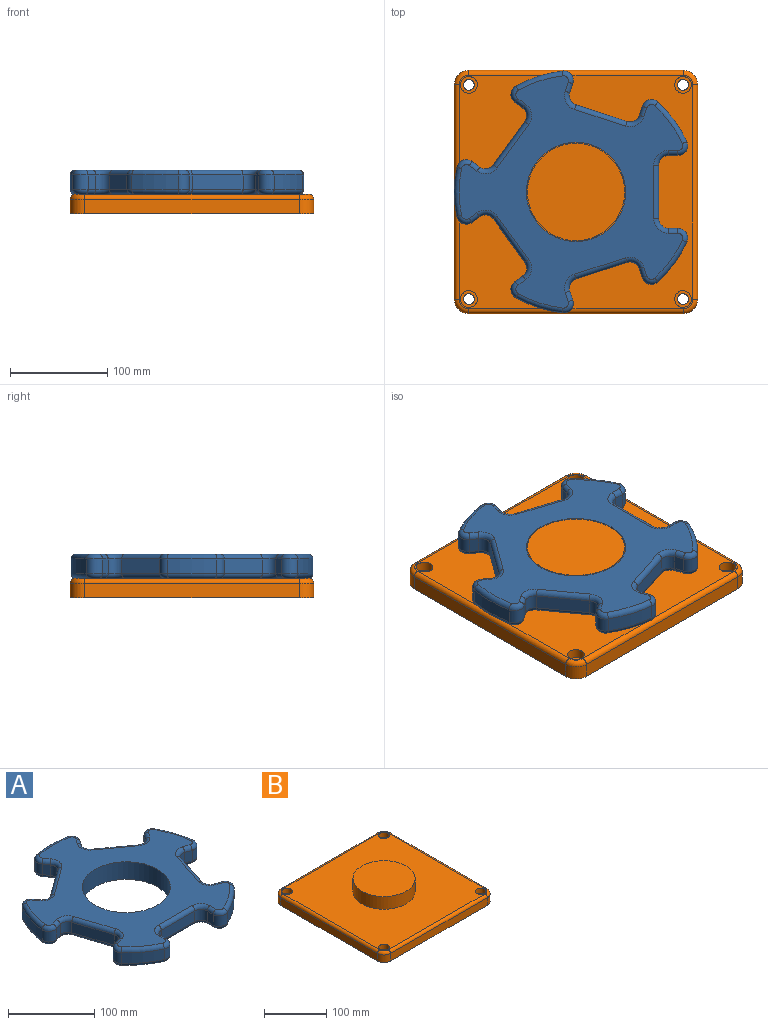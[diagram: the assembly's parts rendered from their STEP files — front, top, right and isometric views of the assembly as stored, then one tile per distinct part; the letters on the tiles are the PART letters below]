
ASSEMBLY  parts=2 mates=1
PART A: 123 faces, bbox 268.9x258.5x25 mm
  f0: plane 238.57x229.73mm, normal (0,0,1), area 21505.7mm2, adj f6,f43,f44,f45,f46,f47,f48,f49
  f1: plane 238.57x229.73mm, normal (0,0,-1), area 21505.7mm2, adj f6,f83,f84,f85,f86,f87,f88,f89
  f2: cylinder r=125mm len=40.68mm, axis (0,0,-1), area 759.5mm2, adj f13,f42,f51,f91
  f3: cylinder r=125mm len=47.82mm, axis (0,0,-1), area 759.5mm2, adj f35,f41,f67,f107
  f4: cylinder r=125mm len=50.29mm, axis (0,0,-1), area 759.5mm2, adj f28,f34,f82,f122
  f5: cylinder r=125mm len=47.82mm, axis (0,0,-1), area 759.5mm2, adj f21,f27,f66,f106
  f6: cylinder r=51mm len=102mm, axis (0,0,-1), area 8011.1mm2, adj f0,f1
  f7: cylinder r=125mm len=40.68mm, axis (0,0,-1), area 759.5mm2, adj f14,f20,f50,f90
  f8: plane 15x9.73mm, normal (-1,0,0), area 146mm2, adj f11,f14,f46,f86
  f9: plane 55x15mm, normal (0,-1,0), area 825mm2, adj f11,f12,f43,f83
  f10: plane 15x9.73mm, normal (1,0,0), area 146mm2, adj f12,f13,f47,f87
  f11: cylinder r=10mm len=15mm, axis (0,0,-1), area 235.6mm2, adj f8,f9,f44,f84
  f12: cylinder r=10mm len=15mm, axis (0,0,-1), area 235.6mm2, adj f9,f10,f45,f85
  f13: cylinder r=10mm len=15mm, axis (0,0,-1), area 299.5mm2, adj f2,f10,f49,f89
  f14: cylinder r=10mm len=15mm, axis (0,0,-1), area 299.5mm2, adj f7,f8,f48,f88
  f15: plane 15x9.26mm, normal (-0.31,-0.95,0), area 146mm2, adj f18,f21,f62,f102
  f16: plane 52.31x17mm, normal (0.95,-0.31,0), area 825mm2, adj f18,f19,f58,f98
  f17: plane 15x9.26mm, normal (0.31,0.95,0), area 146mm2, adj f19,f20,f54,f94
  f18: cylinder r=10mm len=15mm, axis (0,0,-1), area 235.6mm2, adj f15,f16,f60,f100
  f19: cylinder r=10mm len=15mm, axis (0,0,-1), area 235.6mm2, adj f16,f17,f56,f96
  f20: cylinder r=10mm len=16.25mm, axis (0,0,-1), area 299.5mm2, adj f7,f17,f52,f92
  f21: cylinder r=10mm len=15mm, axis (0,0,-1), area 299.5mm2, adj f5,f15,f64,f104
  f22: plane 15x7.87mm, normal (0.81,-0.59,0), area 146mm2, adj f25,f28,f78,f118
  f23: plane 44.5x32.33mm, normal (0.59,0.81,0), area 825mm2, adj f25,f26,f74,f114
  f24: plane 15x7.87mm, normal (-0.81,0.59,0), area 146mm2, adj f26,f27,f70,f110
  f25: cylinder r=10mm len=15mm, axis (0,0,-1), area 235.6mm2, adj f22,f23,f76,f116
  f26: cylinder r=10mm len=15mm, axis (0,0,-1), area 235.6mm2, adj f23,f24,f72,f112
  f27: cylinder r=10mm len=16.78mm, axis (0,0,-1), area 299.5mm2, adj f5,f24,f68,f108
  f28: cylinder r=10mm len=15.67mm, axis (0,0,-1), area 299.5mm2, adj f4,f22,f80,f120
  f29: plane 15x7.87mm, normal (0.81,0.59,0), area 146mm2, adj f32,f35,f71,f111
  f30: plane 44.5x32.33mm, normal (-0.59,0.81,0), area 825mm2, adj f32,f33,f75,f115
  f31: plane 15x7.87mm, normal (-0.81,-0.59,0), area 146mm2, adj f33,f34,f79,f119
  f32: cylinder r=10mm len=15mm, axis (0,0,-1), area 235.6mm2, adj f29,f30,f73,f113
  f33: cylinder r=10mm len=15mm, axis (0,0,-1), area 235.6mm2, adj f30,f31,f77,f117
  f34: cylinder r=10mm len=15.67mm, axis (0,0,-1), area 299.5mm2, adj f4,f31,f81,f121
  f35: cylinder r=10mm len=16.78mm, axis (0,0,-1), area 299.5mm2, adj f3,f29,f69,f109
  f36: plane 15x9.26mm, normal (-0.31,0.95,0), area 146mm2, adj f39,f42,f55,f95
  f37: plane 52.31x17mm, normal (-0.95,-0.31,0), area 825mm2, adj f39,f40,f59,f99
  f38: plane 15x9.26mm, normal (0.31,-0.95,0), area 146mm2, adj f40,f41,f63,f103
  f39: cylinder r=10mm len=15mm, axis (0,0,-1), area 235.6mm2, adj f36,f37,f57,f97
  f40: cylinder r=10mm len=15mm, axis (0,0,-1), area 235.6mm2, adj f37,f38,f61,f101
  f41: cylinder r=10mm len=15mm, axis (0,0,-1), area 299.5mm2, adj f3,f38,f65,f105
  f42: cylinder r=10mm len=16.25mm, axis (0,0,-1), area 299.5mm2, adj f2,f36,f53,f93
  f43: cylinder r=5mm len=55mm, axis (1,0,0), area 432mm2, adj f0,f9,f44,f45
  f44: torus R=15mm, axis (0,0,1), area 145.8mm2, adj f0,f11,f43,f46
  f45: torus R=15mm, axis (0,0,1), area 145.8mm2, adj f0,f12,f43,f47
  f46: cylinder r=5mm len=9.73mm, axis (0,-1,0), area 76.4mm2, adj f0,f8,f44,f48
  f47: cylinder r=5mm len=9.73mm, axis (0,1,0), area 76.4mm2, adj f0,f10,f45,f49
  f48: torus R=5mm, axis (0,0,1), area 128.3mm2, adj f0,f14,f46,f50
  f49: torus R=5mm, axis (0,0,1), area 128.3mm2, adj f0,f13,f47,f51
  f50: torus R=120mm, axis (0,0,1), area 391.9mm2, adj f0,f7,f48,f52
  f51: torus R=120mm, axis (0,0,1), area 391.9mm2, adj f0,f2,f49,f53
  f52: torus R=5mm, axis (0,0,1), area 128.3mm2, adj f0,f20,f50,f54
  f53: torus R=5mm, axis (0,0,1), area 128.3mm2, adj f0,f42,f51,f55
  f54: cylinder r=5mm len=10.8mm, axis (-0.95,0.31,0), area 76.4mm2, adj f0,f17,f52,f56
  f55: cylinder r=5mm len=10.8mm, axis (-0.95,-0.31,0), area 76.4mm2, adj f0,f36,f53,f57
  f56: torus R=15mm, axis (0,0,1), area 145.8mm2, adj f0,f19,f54,f58
  f57: torus R=15mm, axis (0,0,1), area 145.8mm2, adj f0,f39,f55,f59
  f58: cylinder r=5mm len=53.85mm, axis (0.31,0.95,0), area 432mm2, adj f0,f16,f56,f60
  f59: cylinder r=5mm len=53.85mm, axis (0.31,-0.95,0), area 432mm2, adj f0,f37,f57,f61
  f60: torus R=15mm, axis (0,0,1), area 145.8mm2, adj f0,f18,f58,f62
  f61: torus R=15mm, axis (0,0,1), area 145.8mm2, adj f0,f40,f59,f63
  f62: cylinder r=5mm len=10.8mm, axis (0.95,-0.31,0), area 76.4mm2, adj f0,f15,f60,f64
  f63: cylinder r=5mm len=10.8mm, axis (0.95,0.31,0), area 76.4mm2, adj f0,f38,f61,f65
  f64: torus R=5mm, axis (0,0,1), area 128.3mm2, adj f0,f21,f62,f66
  f65: torus R=5mm, axis (0,0,1), area 128.3mm2, adj f0,f41,f63,f67
  f66: torus R=120mm, axis (0,0,1), area 391.9mm2, adj f0,f5,f64,f68
  f67: torus R=120mm, axis (0,0,1), area 391.9mm2, adj f0,f3,f65,f69
  f68: torus R=5mm, axis (0,0,1), area 128.3mm2, adj f0,f27,f66,f70
  f69: torus R=5mm, axis (0,0,1), area 128.3mm2, adj f0,f35,f67,f71
  f70: cylinder r=5mm len=10.81mm, axis (-0.59,-0.81,0), area 76.4mm2, adj f0,f24,f68,f72
  f71: cylinder r=5mm len=10.81mm, axis (-0.59,0.81,0), area 76.4mm2, adj f0,f29,f69,f73
  f72: torus R=15mm, axis (0,0,1), area 145.8mm2, adj f0,f26,f70,f74
  f73: torus R=15mm, axis (0,0,1), area 145.8mm2, adj f0,f32,f71,f75
  f74: cylinder r=5mm len=47.44mm, axis (-0.81,0.59,0), area 432mm2, adj f0,f23,f72,f76
  f75: cylinder r=5mm len=47.44mm, axis (-0.81,-0.59,0), area 432mm2, adj f0,f30,f73,f77
  f76: torus R=15mm, axis (0,0,1), area 145.8mm2, adj f0,f25,f74,f78
  f77: torus R=15mm, axis (0,0,1), area 145.8mm2, adj f0,f33,f75,f79
  f78: cylinder r=5mm len=10.81mm, axis (0.59,0.81,0), area 76.4mm2, adj f0,f22,f76,f80
  f79: cylinder r=5mm len=10.81mm, axis (0.59,-0.81,0), area 76.4mm2, adj f0,f31,f77,f81
  f80: torus R=5mm, axis (0,0,1), area 128.3mm2, adj f0,f28,f78,f82
  f81: torus R=5mm, axis (0,0,1), area 128.3mm2, adj f0,f34,f79,f82
  f82: torus R=120mm, axis (0,0,1), area 391.9mm2, adj f0,f4,f80,f81
  f83: cylinder r=5mm len=55mm, axis (-1,0,0), area 432mm2, adj f1,f9,f84,f85
  f84: torus R=15mm, axis (0,0,1), area 145.8mm2, adj f1,f11,f83,f86
  f85: torus R=15mm, axis (0,0,1), area 145.8mm2, adj f1,f12,f83,f87
  f86: cylinder r=5mm len=9.73mm, axis (0,1,0), area 76.4mm2, adj f1,f8,f84,f88
  f87: cylinder r=5mm len=9.73mm, axis (0,-1,0), area 76.4mm2, adj f1,f10,f85,f89
  f88: torus R=5mm, axis (0,0,1), area 128.3mm2, adj f1,f14,f86,f90
  f89: torus R=5mm, axis (0,0,1), area 128.3mm2, adj f1,f13,f87,f91
  f90: torus R=120mm, axis (0,0,1), area 391.9mm2, adj f1,f7,f88,f92
  f91: torus R=120mm, axis (0,0,1), area 391.9mm2, adj f1,f2,f89,f93
  f92: torus R=5mm, axis (0,0,1), area 128.3mm2, adj f1,f20,f90,f94
  f93: torus R=5mm, axis (0,0,1), area 128.3mm2, adj f1,f42,f91,f95
  f94: cylinder r=5mm len=10.8mm, axis (0.95,-0.31,0), area 76.4mm2, adj f1,f17,f92,f96
  f95: cylinder r=5mm len=10.8mm, axis (0.95,0.31,0), area 76.4mm2, adj f1,f36,f93,f97
  f96: torus R=15mm, axis (0,0,1), area 145.8mm2, adj f1,f19,f94,f98
  f97: torus R=15mm, axis (0,0,1), area 145.8mm2, adj f1,f39,f95,f99
  f98: cylinder r=5mm len=53.85mm, axis (-0.31,-0.95,0), area 432mm2, adj f1,f16,f96,f100
  f99: cylinder r=5mm len=53.85mm, axis (-0.31,0.95,0), area 432mm2, adj f1,f37,f97,f101
  f100: torus R=15mm, axis (0,0,1), area 145.8mm2, adj f1,f18,f98,f102
  f101: torus R=15mm, axis (0,0,1), area 145.8mm2, adj f1,f40,f99,f103
  f102: cylinder r=5mm len=10.8mm, axis (-0.95,0.31,0), area 76.4mm2, adj f1,f15,f100,f104
  f103: cylinder r=5mm len=10.8mm, axis (-0.95,-0.31,0), area 76.4mm2, adj f1,f38,f101,f105
  f104: torus R=5mm, axis (0,0,1), area 128.3mm2, adj f1,f21,f102,f106
  f105: torus R=5mm, axis (0,0,1), area 128.3mm2, adj f1,f41,f103,f107
  f106: torus R=120mm, axis (0,0,1), area 391.9mm2, adj f1,f5,f104,f108
  f107: torus R=120mm, axis (0,0,1), area 391.9mm2, adj f1,f3,f105,f109
  f108: torus R=5mm, axis (0,0,1), area 128.3mm2, adj f1,f27,f106,f110
  f109: torus R=5mm, axis (0,0,1), area 128.3mm2, adj f1,f35,f107,f111
  f110: cylinder r=5mm len=10.81mm, axis (0.59,0.81,0), area 76.4mm2, adj f1,f24,f108,f112
  f111: cylinder r=5mm len=10.81mm, axis (0.59,-0.81,0), area 76.4mm2, adj f1,f29,f109,f113
  f112: torus R=15mm, axis (0,0,1), area 145.8mm2, adj f1,f26,f110,f114
  f113: torus R=15mm, axis (0,0,1), area 145.8mm2, adj f1,f32,f111,f115
  f114: cylinder r=5mm len=47.44mm, axis (0.81,-0.59,0), area 432mm2, adj f1,f23,f112,f116
  f115: cylinder r=5mm len=47.44mm, axis (0.81,0.59,0), area 432mm2, adj f1,f30,f113,f117
  f116: torus R=15mm, axis (0,0,1), area 145.8mm2, adj f1,f25,f114,f118
  f117: torus R=15mm, axis (0,0,1), area 145.8mm2, adj f1,f33,f115,f119
  f118: cylinder r=5mm len=10.81mm, axis (-0.59,-0.81,0), area 76.4mm2, adj f1,f22,f116,f120
  f119: cylinder r=5mm len=10.81mm, axis (-0.59,0.81,0), area 76.4mm2, adj f1,f31,f117,f121
  f120: torus R=5mm, axis (0,0,1), area 128.3mm2, adj f1,f28,f118,f122
  f121: torus R=5mm, axis (0,0,1), area 128.3mm2, adj f1,f34,f119,f122
  f122: torus R=120mm, axis (0,0,1), area 391.9mm2, adj f1,f4,f120,f121
PART B: 32 faces, bbox 252.5x252.5x45 mm
  f0: plane 220x15mm, normal (1,0,0), area 3300mm2, adj f5,f8,f11,f27
  f1: plane 220x15mm, normal (0,1,0), area 3300mm2, adj f5,f8,f9,f31
  f2: plane 220x15mm, normal (-1,0,0), area 3300mm2, adj f5,f9,f10,f28
  f3: plane 220x15mm, normal (0,-1,0), area 3300mm2, adj f5,f10,f11,f24
  f4: plane 240x240mm, normal (0,0,1), area 48725.4mm2, adj f6,f14,f17,f20,f23,f24,f25,f26
  f5: plane 250x250mm, normal (0,0,-1), area 61926.7mm2, adj f0,f1,f2,f3,f8,f9,f10,f11
  f6: cylinder r=50mm len=100mm, axis (0,0,-1), area 7854mm2, adj f4,f7
  f7: plane 100x100mm, normal (0,0,1), area 7854mm2, adj f6
  f8: cylinder r=15mm len=15mm, axis (0,0,-1), area 353.4mm2, adj f0,f1,f5,f29
  f9: cylinder r=15mm len=15mm, axis (0,0,1), area 353.4mm2, adj f1,f2,f5,f30
  f10: cylinder r=15mm len=15mm, axis (0,0,-1), area 353.4mm2, adj f2,f3,f5,f26
  f11: cylinder r=15mm len=15mm, axis (0,0,1), area 353.4mm2, adj f0,f3,f5,f25
  f12: cylinder r=5.5mm len=11mm, axis (0,0,1), area 345.6mm2, adj f5,f13
  f13: plane 17.25x17.25mm, normal (0,0,1), area 138.7mm2, adj f12,f14
  f14: cylinder r=8.62mm len=17.25mm, axis (0,0,1), area 541.9mm2, adj f4,f13
  f15: cylinder r=5.5mm len=11mm, axis (0,0,1), area 345.6mm2, adj f5,f16
  f16: plane 17.25x17.25mm, normal (0,0,1), area 138.7mm2, adj f15,f17
  f17: cylinder r=8.62mm len=17.25mm, axis (0,0,1), area 541.9mm2, adj f4,f16
  f18: cylinder r=5.5mm len=11mm, axis (0,0,1), area 345.6mm2, adj f5,f19
  f19: plane 17.25x17.25mm, normal (0,0,1), area 138.7mm2, adj f18,f20
  f20: cylinder r=8.62mm len=17.25mm, axis (0,0,1), area 541.9mm2, adj f4,f19
  f21: cylinder r=5.5mm len=11mm, axis (0,0,1), area 345.6mm2, adj f5,f22
  f22: plane 17.25x17.25mm, normal (0,0,1), area 138.7mm2, adj f21,f23
  f23: cylinder r=8.62mm len=17.25mm, axis (0,0,1), area 541.9mm2, adj f4,f22
  f24: cylinder r=5mm len=220mm, axis (-1,0,0), area 1727.9mm2, adj f3,f4,f25,f26
  f25: torus R=10mm, axis (0,0,1), area 162.6mm2, adj f4,f11,f24,f27
  f26: torus R=10mm, axis (0,0,1), area 162.6mm2, adj f4,f10,f24,f28
  f27: cylinder r=5mm len=220mm, axis (0,-1,0), area 1727.9mm2, adj f0,f4,f25,f29
  f28: cylinder r=5mm len=220mm, axis (0,1,0), area 1727.9mm2, adj f2,f4,f26,f30
  f29: torus R=10mm, axis (0,0,1), area 162.6mm2, adj f4,f8,f27,f31
  f30: torus R=10mm, axis (0,0,1), area 162.6mm2, adj f4,f9,f28,f31
  f31: cylinder r=5mm len=220mm, axis (1,0,0), area 1727.9mm2, adj f1,f4,f29,f30
PLACE A rot(axis=(0,0,1),90deg) t=(-4.64,-5.72,-29.35)mm
PLACE B t=(-4.64,-5.72,-29.35)mm fixed
MATE revolute B.f6 <-> A.f2  axis (0,0,1) through (-4.64,-5.72,15.65)mm
